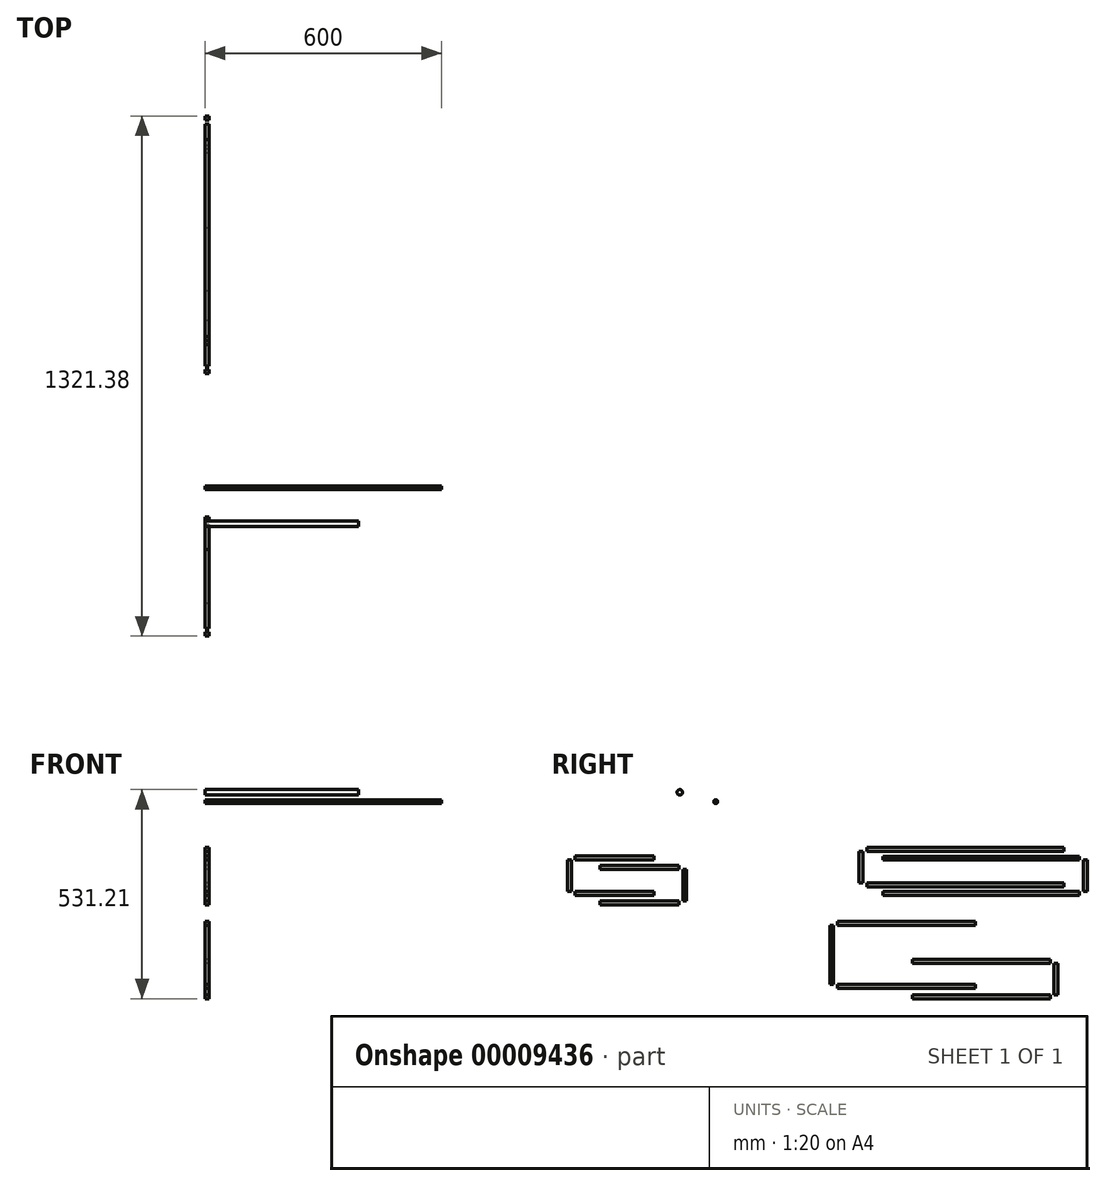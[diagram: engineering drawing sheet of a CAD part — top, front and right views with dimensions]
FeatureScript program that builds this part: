
annotation { "Feature Type Name" : "Feature", "Feature Type Description" : "" }
export const myFeature = defineFeature(function(context is Context, id is Id, definition is map)
    precondition{}
    {
        {
            var Q0;
            Q0=qCreatedBy(makeId("Right.planeOp"),FACE);
            var sketch = newSketch(context, id + "F0", { "sketchPlane" : qUnion([Q0])});
            skLineSegment(sketch, "E0.bottom", {"start": v(-89.52, 73.22) * mm, "end": v(-79.52, 73.22) * mm});
            skLineSegment(sketch, "E0.top", {"start": v(-89.52, -6.78) * mm, "end": v(-79.52, -6.78) * mm});
            skLineSegment(sketch, "E0.left", {"start": v(-89.52, 73.22) * mm, "end": v(-89.52, -6.78) * mm});
            skLineSegment(sketch, "E0.right", {"start": v(-79.52, 73.22) * mm, "end": v(-79.52, -6.78) * mm});
            skLineSegment(sketch, "E1.bottom", {"start": v(-69.52, 73.22) * mm, "end": v(430.48, 73.22) * mm});
            skLineSegment(sketch, "E1.top", {"start": v(-69.52, 83.22) * mm, "end": v(430.48, 83.22) * mm});
            skLineSegment(sketch, "E1.left", {"start": v(-69.52, 73.22) * mm, "end": v(-69.52, 83.22) * mm});
            skLineSegment(sketch, "E1.right", {"start": v(430.48, 73.22) * mm, "end": v(430.48, 83.22) * mm});
            skLineSegment(sketch, "E2.bottom", {"start": v(480.59, 50.91) * mm, "end": v(490.59, 50.91) * mm});
            skLineSegment(sketch, "E2.top", {"start": v(480.59, -29.09) * mm, "end": v(490.59, -29.09) * mm});
            skLineSegment(sketch, "E2.left", {"start": v(480.59, 50.91) * mm, "end": v(480.59, -29.09) * mm});
            skLineSegment(sketch, "E2.right", {"start": v(490.59, 50.91) * mm, "end": v(490.59, -29.09) * mm});
            skLineSegment(sketch, "E3.bottom", {"start": v(470.59, 50.91) * mm, "end": v(-29.41, 50.91) * mm});
            skLineSegment(sketch, "E3.top", {"start": v(470.59, 60.91) * mm, "end": v(-29.41, 60.91) * mm});
            skLineSegment(sketch, "E3.left", {"start": v(470.59, 50.91) * mm, "end": v(470.59, 60.91) * mm});
            skLineSegment(sketch, "E3.right", {"start": v(-29.41, 50.91) * mm, "end": v(-29.41, 60.91) * mm});
            skLineSegment(sketch, "E4.bottom", {"start": v(-69.52, -6.78) * mm, "end": v(430.48, -6.78) * mm});
            skLineSegment(sketch, "E4.top", {"start": v(-69.52, -16.78) * mm, "end": v(430.48, -16.78) * mm});
            skLineSegment(sketch, "E4.left", {"start": v(-69.52, -6.78) * mm, "end": v(-69.52, -16.78) * mm});
            skLineSegment(sketch, "E4.right", {"start": v(430.48, -6.78) * mm, "end": v(430.48, -16.78) * mm});
            skLineSegment(sketch, "E5.bottom", {"start": v(470.59, -29.09) * mm, "end": v(-29.41, -29.09) * mm});
            skLineSegment(sketch, "E5.top", {"start": v(470.59, -39.09) * mm, "end": v(-29.41, -39.09) * mm});
            skLineSegment(sketch, "E5.left", {"start": v(470.59, -29.09) * mm, "end": v(470.59, -39.09) * mm});
            skLineSegment(sketch, "E5.right", {"start": v(-29.41, -29.09) * mm, "end": v(-29.41, -39.09) * mm});
            skSolve(sketch);
        }
        {
            var Q0;
            Q0 = qSketchRegion(id + "F0", true);
            extrude(context, id + "F1", {"entities" : qUnion([Q0]), "depth" : 10 * mm});
        }
        {
            var Q0;
            Q0=qCreatedBy(makeId("Right.planeOp"),FACE);
            var sketch = newSketch(context, id + "F2", { "sketchPlane" : qUnion([Q0])});
            skLineSegment(sketch, "E6.bottom", {"start": v(-164.15, -114.36) * mm, "end": v(-154.15, -114.36) * mm});
            skLineSegment(sketch, "E6.top", {"start": v(-164.15, -264.36) * mm, "end": v(-154.15, -264.36) * mm});
            skLineSegment(sketch, "E6.left", {"start": v(-164.15, -114.36) * mm, "end": v(-164.15, -264.36) * mm});
            skLineSegment(sketch, "E6.right", {"start": v(-154.15, -114.36) * mm, "end": v(-154.15, -264.36) * mm});
            skLineSegment(sketch, "E7.bottom", {"start": v(-144.15, -114.36) * mm, "end": v(205.85, -114.36) * mm});
            skLineSegment(sketch, "E7.top", {"start": v(-144.15, -104.36) * mm, "end": v(205.85, -104.36) * mm});
            skLineSegment(sketch, "E7.left", {"start": v(-144.15, -114.36) * mm, "end": v(-144.15, -104.36) * mm});
            skLineSegment(sketch, "E7.right", {"start": v(205.85, -114.36) * mm, "end": v(205.85, -104.36) * mm});
            skLineSegment(sketch, "E8.bottom", {"start": v(405.95, -211.05) * mm, "end": v(415.95, -211.05) * mm});
            skLineSegment(sketch, "E8.top", {"start": v(405.95, -291.05) * mm, "end": v(415.95, -291.05) * mm});
            skLineSegment(sketch, "E8.left", {"start": v(405.95, -211.05) * mm, "end": v(405.95, -291.05) * mm});
            skLineSegment(sketch, "E8.right", {"start": v(415.95, -211.05) * mm, "end": v(415.95, -291.05) * mm});
            skLineSegment(sketch, "E9.bottom", {"start": v(395.95, -211.05) * mm, "end": v(45.95, -211.05) * mm});
            skLineSegment(sketch, "E9.top", {"start": v(395.95, -201.05) * mm, "end": v(45.95, -201.05) * mm});
            skLineSegment(sketch, "E9.left", {"start": v(395.95, -211.05) * mm, "end": v(395.95, -201.05) * mm});
            skLineSegment(sketch, "E9.right", {"start": v(45.95, -211.05) * mm, "end": v(45.95, -201.05) * mm});
            skLineSegment(sketch, "E10.bottom", {"start": v(-144.15, -264.36) * mm, "end": v(205.85, -264.36) * mm});
            skLineSegment(sketch, "E10.top", {"start": v(-144.15, -274.36) * mm, "end": v(205.85, -274.36) * mm});
            skLineSegment(sketch, "E10.left", {"start": v(-144.15, -264.36) * mm, "end": v(-144.15, -274.36) * mm});
            skLineSegment(sketch, "E10.right", {"start": v(205.85, -264.36) * mm, "end": v(205.85, -274.36) * mm});
            skLineSegment(sketch, "E11.bottom", {"start": v(395.95, -291.05) * mm, "end": v(45.95, -291.05) * mm});
            skLineSegment(sketch, "E11.top", {"start": v(395.95, -301.05) * mm, "end": v(45.95, -301.05) * mm});
            skLineSegment(sketch, "E11.left", {"start": v(395.95, -291.05) * mm, "end": v(395.95, -301.05) * mm});
            skLineSegment(sketch, "E11.right", {"start": v(45.95, -291.05) * mm, "end": v(45.95, -301.05) * mm});
            skSolve(sketch);
        }
        {
            var Q0;
            Q0 = qSketchRegion(id + "F2", true);
            extrude(context, id + "F3", {"entities" : qUnion([Q0]), "depth" : 10 * mm});
        }
        {
            var Q0;
            Q0=qCreatedBy(makeId("Right.planeOp"),FACE);
            var sketch = newSketch(context, id + "F4", { "sketchPlane" : qUnion([Q0])});
            skLineSegment(sketch, "E12.bottom", {"start": v(-830.8, 51.15) * mm, "end": v(-820.8, 51.15) * mm});
            skLineSegment(sketch, "E12.top", {"start": v(-830.8, -28.85) * mm, "end": v(-820.8, -28.85) * mm});
            skLineSegment(sketch, "E12.left", {"start": v(-830.8, 51.15) * mm, "end": v(-830.8, -28.85) * mm});
            skLineSegment(sketch, "E12.right", {"start": v(-820.8, 51.15) * mm, "end": v(-820.8, -28.85) * mm});
            skLineSegment(sketch, "E13.bottom", {"start": v(-810.8, 51.15) * mm, "end": v(-610.8, 51.15) * mm});
            skLineSegment(sketch, "E13.top", {"start": v(-810.8, 61.15) * mm, "end": v(-610.8, 61.15) * mm});
            skLineSegment(sketch, "E13.left", {"start": v(-810.8, 51.15) * mm, "end": v(-810.8, 61.15) * mm});
            skLineSegment(sketch, "E13.right", {"start": v(-610.8, 51.15) * mm, "end": v(-610.8, 61.15) * mm});
            skLineSegment(sketch, "E14.bottom", {"start": v(-537.58, 27) * mm, "end": v(-527.58, 27) * mm});
            skLineSegment(sketch, "E14.top", {"start": v(-537.58, -53) * mm, "end": v(-527.58, -53) * mm});
            skLineSegment(sketch, "E14.left", {"start": v(-537.58, 27) * mm, "end": v(-537.58, -53) * mm});
            skLineSegment(sketch, "E14.right", {"start": v(-527.58, 27) * mm, "end": v(-527.58, -53) * mm});
            skLineSegment(sketch, "E15.bottom", {"start": v(-547.58, 27) * mm, "end": v(-747.58, 27) * mm});
            skLineSegment(sketch, "E15.top", {"start": v(-547.58, 37) * mm, "end": v(-747.58, 37) * mm});
            skLineSegment(sketch, "E15.left", {"start": v(-547.58, 27) * mm, "end": v(-547.58, 37) * mm});
            skLineSegment(sketch, "E15.right", {"start": v(-747.58, 27) * mm, "end": v(-747.58, 37) * mm});
            skLineSegment(sketch, "E16.bottom", {"start": v(-810.8, -28.85) * mm, "end": v(-610.8, -28.85) * mm});
            skLineSegment(sketch, "E16.top", {"start": v(-810.8, -38.85) * mm, "end": v(-610.8, -38.85) * mm});
            skLineSegment(sketch, "E16.left", {"start": v(-810.8, -28.85) * mm, "end": v(-810.8, -38.85) * mm});
            skLineSegment(sketch, "E16.right", {"start": v(-610.8, -28.85) * mm, "end": v(-610.8, -38.85) * mm});
            skLineSegment(sketch, "E17.bottom", {"start": v(-547.58, -53) * mm, "end": v(-747.58, -53) * mm});
            skLineSegment(sketch, "E17.top", {"start": v(-547.58, -63) * mm, "end": v(-747.58, -63) * mm});
            skLineSegment(sketch, "E17.left", {"start": v(-547.58, -53) * mm, "end": v(-547.58, -63) * mm});
            skLineSegment(sketch, "E17.right", {"start": v(-747.58, -53) * mm, "end": v(-747.58, -63) * mm});
            skSolve(sketch);
        }
        {
            var Q0;
            Q0 = qSketchRegion(id + "F4", true);
            extrude(context, id + "F5", {"entities" : qUnion([Q0]), "depth" : 10 * mm});
        }
        {
            var Q0;
            Q0=qCreatedBy(makeId("Right.planeOp"),FACE);
            var sketch = newSketch(context, id + "F6", { "sketchPlane" : qUnion([Q0])});
            skCircle(sketch, "E18", {"center": v(-453.85, 199.49) * mm, "radius": 5 * mm});
            skSolve(sketch);
        }
        {
            var Q0;
            Q0=makeQuery(id+"F6.imprint","IMPRINT",FACE,{"disambiguationData":[TD([[makeQuery(id+"F6.imprint","IMPRINT",EDGE,{"derivedFrom":sQuery(id+"F6.wireOp",EDGE,"E18")}),1.0]])]});
            extrude(context, id + "F7", {"entities" : qUnion([Q0]), "depth" : 600 * mm});
        }
        {
            var Q0;
            Q0=qCreatedBy(makeId("Right.planeOp"),FACE);
            var sketch = newSketch(context, id + "F8", { "sketchPlane" : qUnion([Q0])});
            skCircle(sketch, "E19", {"center": v(-545.08, 223.16) * mm, "radius": 7 * mm});
            skSolve(sketch);
        }
        {
            var Q0;
            Q0=makeQuery(id+"F8.imprint","IMPRINT",FACE,{"disambiguationData":[TD([[makeQuery(id+"F8.imprint","IMPRINT",EDGE,{"derivedFrom":sQuery(id+"F8.wireOp",EDGE,"E19")}),1.0]])]});
            var Q1;
            Q1=sQuery(id+"F8.wireOp",EDGE,"E19");
            extrude(context, id + "F9", {"entities" : qUnion([Q0]), "surfaceEntities" : qUnion([Q1]), "depth" : 390 * mm});
        }
    });
